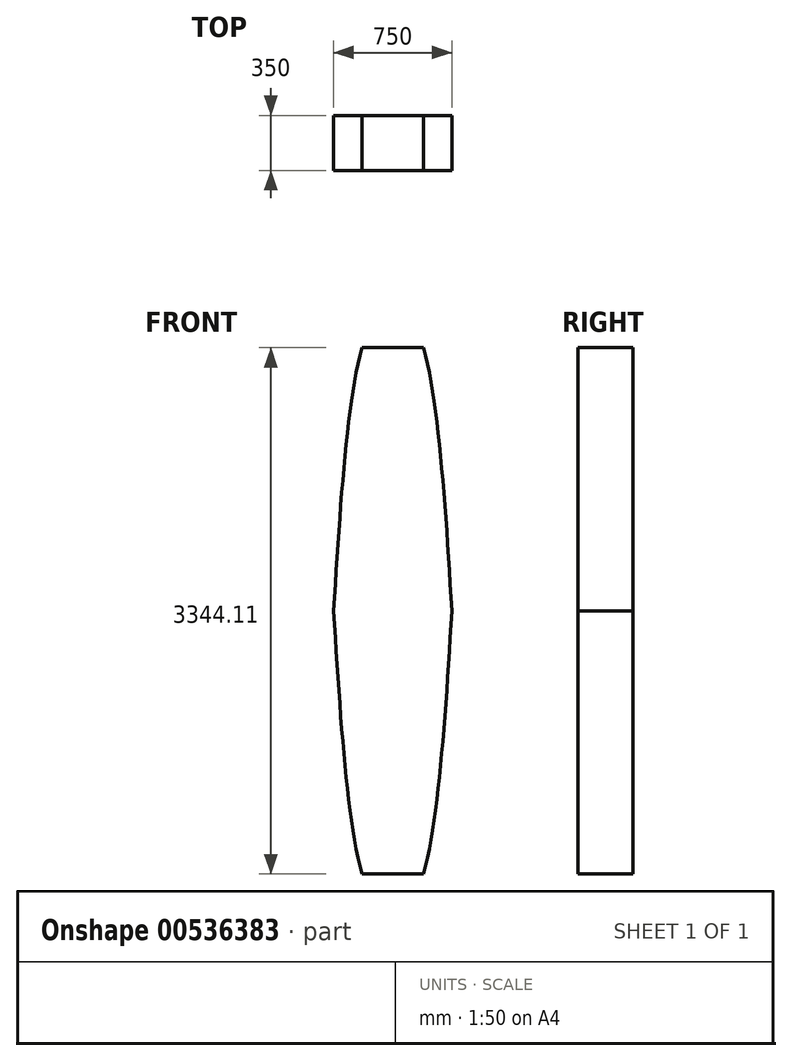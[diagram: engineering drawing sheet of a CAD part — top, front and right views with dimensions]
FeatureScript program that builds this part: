
annotation { "Feature Type Name" : "Feature", "Feature Type Description" : "" }
export const myFeature = defineFeature(function(context is Context, id is Id, definition is map)
    precondition{}
    {
        {
            var Q0;
            Q0=qCreatedBy(makeId("Front.planeOp"),FACE);
            var sketch = newSketch(context, id + "F0", { "sketchPlane" : qUnion([Q0])});
            skFitSpline(sketch, "E0", {"points": [v(-50.3, 7) * mm, v(0, 753.32) * mm, v(60.42, 1324.75) * mm, v(128.92, 1679.06) * mm, v(216.9, 1887.95) * mm, v(324.7, 2007) * mm], "startDerivative": vector(166.55, 2737.71) * mm, "endDerivative": vector(886.17, 835.04) * mm});
            skFitSpline(sketch, "E1.MirrorCS", {"points": [v(699.7, 7) * mm, v(649.38, 753.32) * mm, v(588.96, 1324.75) * mm, v(520.47, 1679.06) * mm, v(432.48, 1887.95) * mm, v(324.7, 2007) * mm], "startDerivative": vector(-166.55, 2737.71) * mm, "endDerivative": vector(-886.17, 835.04) * mm});
            skFitSpline(sketch, "E2.MirrorCS", {"points": [v(-50.3, 7) * mm, v(0, -739.32) * mm, v(60.42, -1310.74) * mm, v(128.92, -1665.05) * mm, v(216.9, -1873.94) * mm, v(324.7, -1993) * mm], "startDerivative": vector(166.55, -2737.71) * mm, "endDerivative": vector(886.17, -835.04) * mm});
            skFitSpline(sketch, "E3.MirrorCS", {"points": [v(699.7, 7) * mm, v(649.38, -739.32) * mm, v(588.96, -1310.74) * mm, v(520.47, -1665.05) * mm, v(432.48, -1873.94) * mm, v(324.7, -1993) * mm], "startDerivative": vector(-166.55, -2737.71) * mm, "endDerivative": vector(-886.17, -835.04) * mm});
            skLineSegment(sketch, "E4", {"start": v(520.47, 1679.06) * mm, "end": v(128.92, 1679.06) * mm});
            skLineSegment(sketch, "E5", {"start": v(128.92, -1665.05) * mm, "end": v(520.47, -1665.05) * mm});
            skLineSegment(sketch, "E6", {"start": v(216.9, -1873.94) * mm, "end": v(432.48, -1873.94) * mm});
            skLineSegment(sketch, "E7", {"start": v(216.9, 1887.95) * mm, "end": v(432.48, 1887.95) * mm});
            skSolve(sketch);
        }
        {
            var Q0;
            {var subQ7=sQuery(id+"F0.wireOp",EDGE,"E4");Q0=makeQuery(id+"F0.imprint","IMPRINT",FACE,{"disambiguationData":[TD([[makeQuery(id+"F0.imprint","IMPRINT",EDGE,{"derivedFrom":subQ7}),1.0]])]});}
            extrude(context, id + "F1", {"entities" : qUnion([Q0]), "depth" : 350 * mm, "offsetDistance" : 25 * mm});
        }
    });
